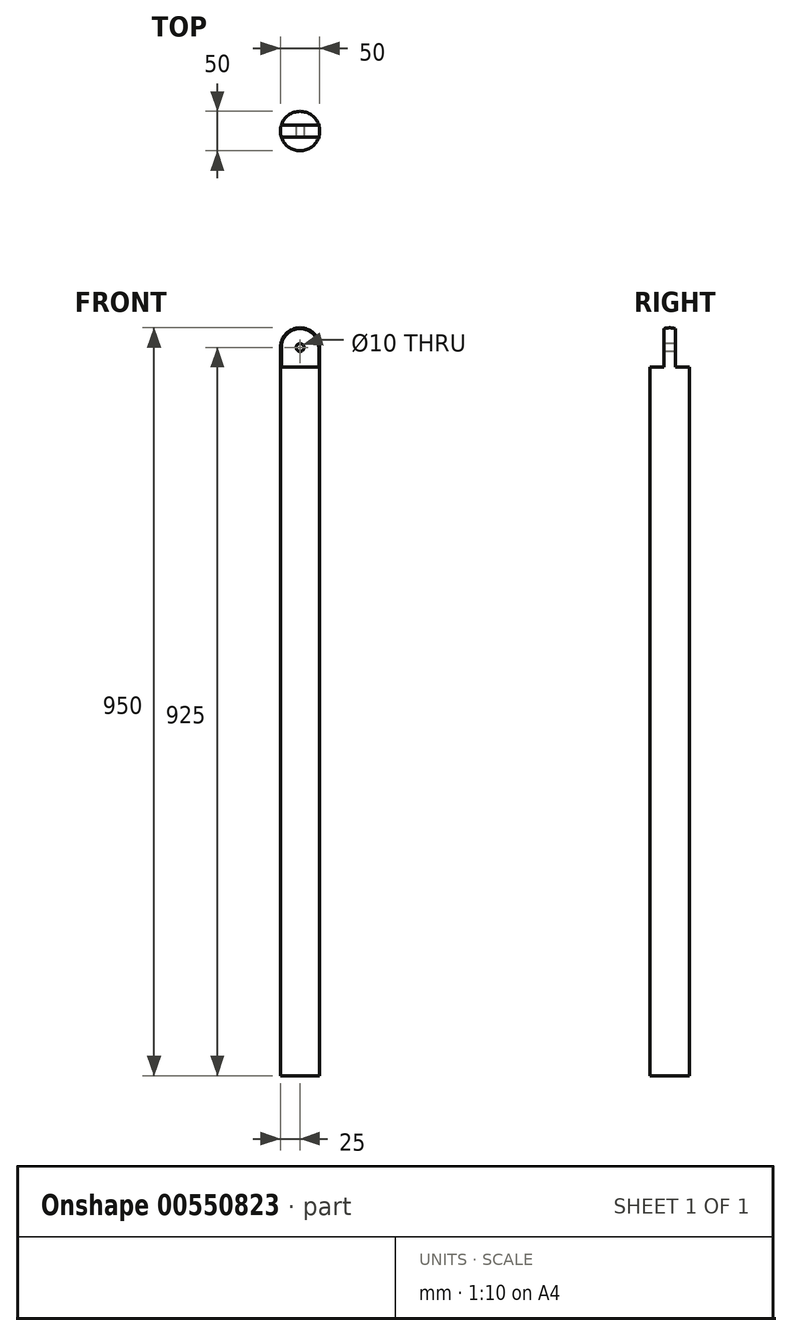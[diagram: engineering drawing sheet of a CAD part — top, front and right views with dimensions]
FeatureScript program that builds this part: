
annotation { "Feature Type Name" : "Feature", "Feature Type Description" : "" }
export const myFeature = defineFeature(function(context is Context, id is Id, definition is map)
    precondition{}
    {
        {
            var Q0;
            Q0=qCreatedBy(makeId("Top.planeOp"),FACE);
            var sketch = newSketch(context, id + "F0", { "sketchPlane" : qUnion([Q0])});
            skCircle(sketch, "E0", {"center": v(0, 0) * mm, "radius": 25 * mm});
            skSolve(sketch);
        }
        {
            var Q0;
            Q0=makeQuery(id+"F0.imprint","IMPRINT",FACE,{"disambiguationData":[TD([[makeQuery(id+"F0.imprint","IMPRINT",EDGE,{"derivedFrom":sQuery(id+"F0.wireOp",EDGE,"E0")}),1.0]])]});
            var Q1;
            Q1=sQuery(id+"F0.wireOp",EDGE,"E0");
            extrude(context, id + "F1", {"entities" : qUnion([Q0]), "surfaceEntities" : qUnion([Q1]), "depth" : 900 * mm, "offsetDistance" : 25 * mm});
        }
        {
            var Q0;
            Q0=makeQuery(id+"F1.opExtrude","CAP_FACE",FACE,{"disambiguationData":[OSD([sQuery(id+"F0.wireOp",EDGE,"E0")])],"isStart":false});
            var sketch = newSketch(context, id + "F2", { "sketchPlane" : qUnion([Q0])});
            skLineSegment(sketch, "E1.bottom", {"start": v(25, -7.5) * mm, "end": v(-25, -7.5) * mm});
            skLineSegment(sketch, "E1.top", {"start": v(25, 7.5) * mm, "end": v(-25, 7.5) * mm});
            skLineSegment(sketch, "E1.left", {"start": v(25, -7.5) * mm, "end": v(25, 7.5) * mm});
            skLineSegment(sketch, "E1.right", {"start": v(-25, -7.5) * mm, "end": v(-25, 7.5) * mm});
            skPoint(sketch, "E1.middle", {"position": v(0, 0) * mm});
            skSolve(sketch);
        }
        {
            var Q0;
            {var subQ0=sQuery(id+"F2.wireOp",EDGE,"E1.bottom");var subQ1=makeQuery(id+"F1.opExtrude","CAP_EDGE",EDGE,{"disambiguationData":[OSD([sQuery(id+"F0.wireOp",EDGE,"E0")])],"isStart":false});var subQ4=makeQuery(id+"F2.imprint","INTERSECT",VERTEX,{"disambiguationData":[OD(0.0)],"derivedFrom":[subQ1,subQ0]});Q0=makeQuery(id+"F2.imprint","IMPRINT",FACE,{"disambiguationData":[TD([[makeQuery(id+"F2.imprint","IMPRINT",EDGE,{"disambiguationData":[TD([[subQ4,-1.0]])],"derivedFrom":subQ0}),-1.0]])]});}
            extrude(context, id + "F3", {"entities" : qUnion([Q0]), "operationType" : NewBodyOperationType.ADD, "depth" : 50 * mm, "offsetDistance" : 25 * mm});
        }
        {
            var Q0;
            {var subQ0=sQuery(id+"F0.wireOp",EDGE,"E0");var subQ1=makeQuery(id+"F1.opExtrude","CAP_EDGE",EDGE,{"disambiguationData":[OSD([subQ0])],"isStart":false});Q0=makeQuery(id+"F3.opExtrude","CAP_EDGE",EDGE,{"disambiguationData":[OSD([subQ0]),TDD([makeQuery(id+"F2.imprint","IMPRINT",EDGE,{"disambiguationData":[TD([[makeQuery(id+"F2.imprint","INTERSECT",VERTEX,{"disambiguationData":[OD(0.0)],"derivedFrom":[subQ1,sQuery(id+"F2.wireOp",EDGE,"E1.bottom")]}),-1.0]])],"derivedFrom":subQ1}),makeQuery(id+"F2.imprint","IMPRINT",EDGE,{"disambiguationData":[TD([[makeQuery(id+"F2.imprint","INTERSECT",VERTEX,{"disambiguationData":[OD(0.0)],"derivedFrom":[subQ1,sQuery(id+"F2.wireOp",EDGE,"E1.top")]}),1.0]])],"derivedFrom":subQ1})])],"isStart":false});}
            fillet(context, id + "F4", {"entities" : qUnion([Q0]), "radius" : 25 * mm, "tangentPropagation" : true, "allowEdgeOverflow" : false});
        }
        {
            var Q0;
            Q0=makeQuery(id+"F3.opExtrude","SWEPT_FACE",FACE,{"disambiguationData":[OSD([sQuery(id+"F2.wireOp",EDGE,"E1.bottom")])]});
            var sketch = newSketch(context, id + "F5", { "sketchPlane" : qUnion([Q0])});
            skCircle(sketch, "E2", {"center": v(0, 925) * mm, "radius": 5 * mm});
            skSolve(sketch);
        }
        {
            var Q0;
            Q0=makeQuery(id+"F5.imprint","IMPRINT",FACE,{"disambiguationData":[TD([[makeQuery(id+"F5.imprint","IMPRINT",EDGE,{"derivedFrom":sQuery(id+"F5.wireOp",EDGE,"E2")}),1.0]])]});
            extrude(context, id + "F6", {"entities" : qUnion([Q0]), "operationType" : NewBodyOperationType.REMOVE, "oppositeDirection" : true, "depth" : 15 * mm, "offsetDistance" : 25 * mm});
        }
    });
